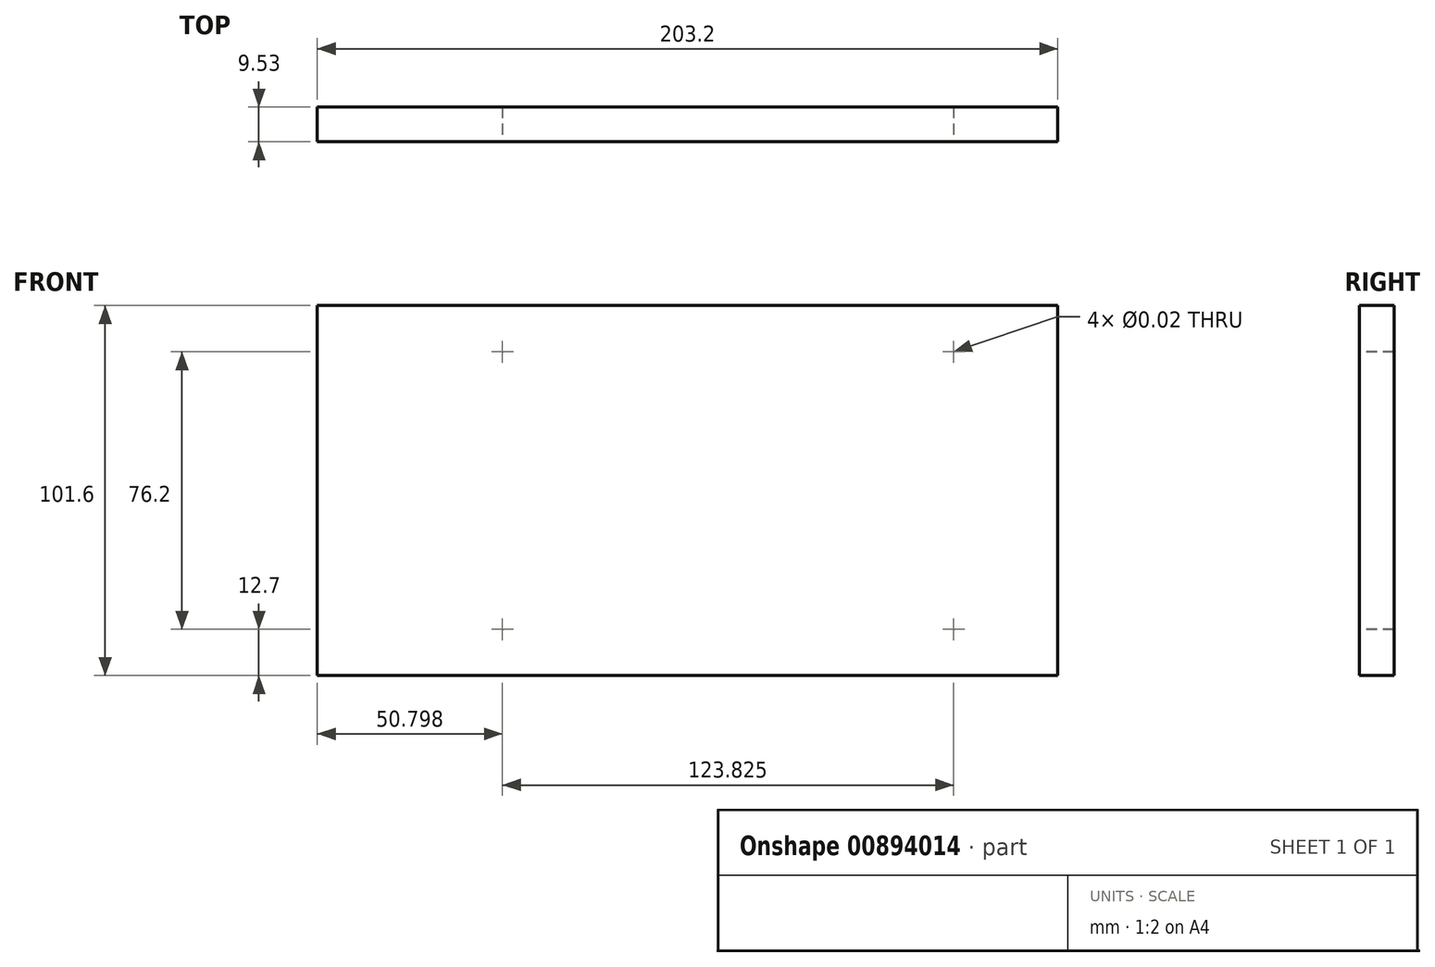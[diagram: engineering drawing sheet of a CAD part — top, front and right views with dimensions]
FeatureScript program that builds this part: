
annotation { "Feature Type Name" : "Feature", "Feature Type Description" : "" }
export const myFeature = defineFeature(function(context is Context, id is Id, definition is map)
    precondition{}
    {
        {
            var Q0;
            Q0=qCreatedBy(makeId("Front.planeOp"),FACE);
            var sketch = newSketch(context, id + "F0", { "sketchPlane" : qUnion([Q0])});
            skLineSegment(sketch, "E0.bottom", {"start": v(-100.13, 50.8) * mm, "end": v(103.07, 50.8) * mm});
            skLineSegment(sketch, "E0.top", {"start": v(-100.13, -50.8) * mm, "end": v(103.07, -50.8) * mm});
            skLineSegment(sketch, "E0.left", {"start": v(-100.13, 50.8) * mm, "end": v(-100.13, -50.8) * mm});
            skLineSegment(sketch, "E0.right", {"start": v(103.07, 50.8) * mm, "end": v(103.07, -50.8) * mm});
            skPoint(sketch, "E0.middle", {"position": v(1.47, 0) * mm});
            skPoint(sketch, "E1", {"position": v(74.5, 38.1) * mm});
            skPoint(sketch, "E2", {"position": v(74.5, -38.1) * mm});
            skPoint(sketch, "E3", {"position": v(-49.33, -38.1) * mm});
            skPoint(sketch, "E4", {"position": v(-49.33, 38.1) * mm});
            skSolve(sketch);
        }
        {
            var Q0;
            Q0 = qSketchRegion(id + "F0", true);
            extrude(context, id + "F1", {"entities" : qUnion([Q0]), "depth" : 9.52 * mm, "offsetDistance" : 25.4 * mm});
        }
        {
            var Q0;
            Q0=sQuery(id+"F0.wireOp",VERTEX,"E1");
            var Q1;
            Q1=sQuery(id+"F0.wireOp",VERTEX,"E3");
            var Q2;
            Q2=sQuery(id+"F0.wireOp",VERTEX,"E4");
            var Q3;
            Q3=sQuery(id+"F0.wireOp",VERTEX,"E2");
            var Q4;
            Q4=makeQuery(id+"F1.opExtrude","SWEPT_BODY",BODY,{"disambiguationData":[OSD([sQuery(id+"F0.wireOp",EDGE,"E0.bottom"),sQuery(id+"F0.wireOp",EDGE,"E0.top"),sQuery(id+"F0.wireOp",EDGE,"E0.left"),sQuery(id+"F0.wireOp",EDGE,"E0.right")])]});
            hole(context, id + "F2", {"style" : HoleStyle.SIMPLE, "endStyle" : HoleEndStyle.BLIND, "oppositeDirection" : true, "standardTappedOrClearance" : lookupTablePath({ "standard" : "ANSI", "size" : "7/16 (0.44)", "type" : "Drilled" }), "standardBlindInLast" : lookupTablePath({ "standard" : "ANSI", "size" : "7/16", "type" : "Drilled" }), "holeDiameter" : 7 / 406.4 * mm, "majorDiameter" : 9.52 * mm, "holeDepth" : 19.05 * mm, "isTappedThrough" : true, "tappedDepth" : 14.29 * mm, "tapClearance" : 3, "locations" : qUnion([Q0, Q1, Q2, Q3]), "scope" : qUnion([Q4]), "startStyle" : HoleStartStyle.SKETCH});
        }
    });
